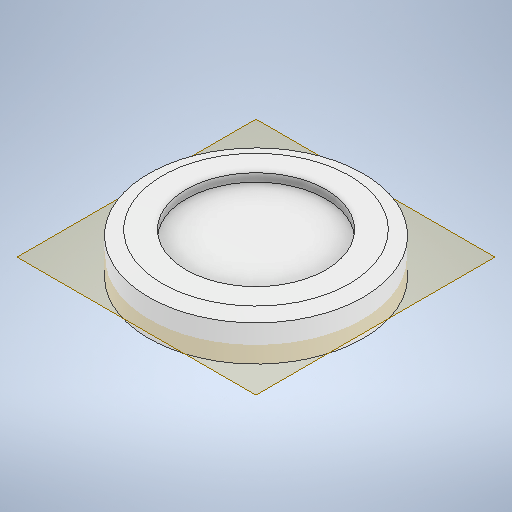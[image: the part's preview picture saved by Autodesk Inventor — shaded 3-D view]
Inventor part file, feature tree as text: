
AUTODESK INVENTOR PART (.ipt)
format: ipt  version: 2025.1 (Build 291241020, 241B)  size: 623,104 bytes
history: native  units: in
note: dims shown in document units (in); Inventor stores cm internally (conversion verified against a paired STEP export)
features: extrude x4, sketch x4, chamfer x2, plane x1, mirror x1
ambient origin geometry x8: Origin, YZ Plane, XZ Plane, XY Plane, X Axis, Y Axis, Z Axis, Center Point
bodies: Solid1 (feature_tree)
feature tree (12):
  extrude  "Extrusion1"  Depth=1.0in
  plane  "Work Plane1"
  extrude  "Extrusion2"  Depth=0.0472in
  extrude  "Extrusion3"  Depth=0.0112in TaperAngle=0.0deg
  extrude  "Extrusion4"  Depth=0.0787in
  chamfer  "Chamfer1"  [1 undecoded]
  chamfer  "Chamfer2"  [1 undecoded]
  sketch  "Sketch1"  dims[d0=1.0in d1=0.0in d2=0.8071in]
  sketch  "Sketch2"  dims[d3=0.0472in d4=0.0in d5=1.2402in]
  sketch  "Sketch3"  dims[d6=0.0in d7=0.0in d8=0.0112in d9=0.0in]
  sketch  "Sketch4"  dims[d10=0.0787in d11=0.0787in d12=0.1374in d13=0.0787in d14=0.0787in d15=0.1374in]
  mirror  "Mirror1"
note: 2 required parameter values undecoded (feature->parameter linkage not recoverable at this tier; creation-order binding heuristic only, values carry confidence <= 0.55)
